# Revit family: LUXI_WATERPROOF LIGHT_HR
name_source: partatom
category: Apparecchi per illuminazione
revit_build: Autodesk Revit 2016 (Build: 20161004_0715(x64)
units: mm (PartAtom-declared; Revit-internal decimal feet)

## family parameters
Condiviso = No
Host = Superficie
Numero OmniClass = 23.80.70.00
Punto di calcolo locali = Sì
Quota connettore circolare = Usa diametro
Sorgente d'illuminazione = Sì
Taglio con vuoti quando caricato = No
Tipo di parte = Normale
Titolo OmniClass = Lighting

## types (2) — shared parameters
Alimentatore = Incluso
Alimentazione = 220-240V AC / 50-60 Hz
Angolo inclinazione = -90.00°
Carico apparente = 80 VA
Certificazioni = CE / RohS
Classe di efficienza energetica = A+
Classe di protezione = I
Classe di rischio fotobiologico = Esente (RG0)
Colore = Nero
Descrizione = Plafoniera stagna
Dimensioni = 1490x78x96
Emetti da larghezza rettangolo = 81 mm  [stored 0.265748 ft]
Emetti da lunghezza rettangolo = 1450 mm  [stored 4.75722 ft]
Fattore di correzione di potenza = ≥0,95 (typ.)
File diagramma fotometrico = WPHR080150BG840K Luxi SERIE HR 80W 4000K.IES
Filtro dei colori = 16777215
Garanzia = 3 anni
Grado di protezione = IP 69K
H = 78 mm  [stored 0.255906 ft]
IFCExportAs = IfcLightFixtureType
Indice di resa cromatica = ≥80 (typ.)
Larghezza = 96 mm  [stored 0.314961 ft]
Lunghezza = 1490 mm  [stored 4.88845 ft]
Masterformat 2016 Codice = 26.50.00
Masterformat 2016 Descrizione = Lighting
Materiale 1 = Acciao INOX 316_Nero
Materiale 3 = Alluminio_Nero
Modello = Serie HR | Waterproof Light
Ottiche = Diffondente
Peso = 4.50 kg
Potenza = 80 W
Produttore = Luxi Illuminazione S.r.l.
Prospetto di default = 2000 mm  [stored 6.56168 ft]
Protezione agli urti = IK10 (20 Joule)
Regolazione del flusso luminoso = Non disponibile
Rendi la forma visibile nel rendering = No
Revisione = 3
Sistema di illuminazione = luce diretta
Sorgente = LED SMD
Step MacAdam (SDCM) = <4
Temperatura di esercizio = -40°C / +45°C
Tipologie di installazione = Sospensione / soffitto
URL = https://www.luxi.lighting
Uniclass 2015 Codice = EF_70_80
Uniclass 2015 Descrizione = Lighting
Variazione temperatura colore lampada con luminosità attenuata = <Nessuno>
Vita utile = L70B20 50.000ore

## per-type parameters (varying)
| type | Materiale 2 |
| WPHR080150BG840K | Vetro Temperato |
| WPHR080150BP840K | PMMA Acrilico |

note: column(s) folded — value = type name in every type: Articolo

note: [stored X ft] marks values corroborated as IEEE doubles in the binary element streams (Revit-internal decimal feet)
